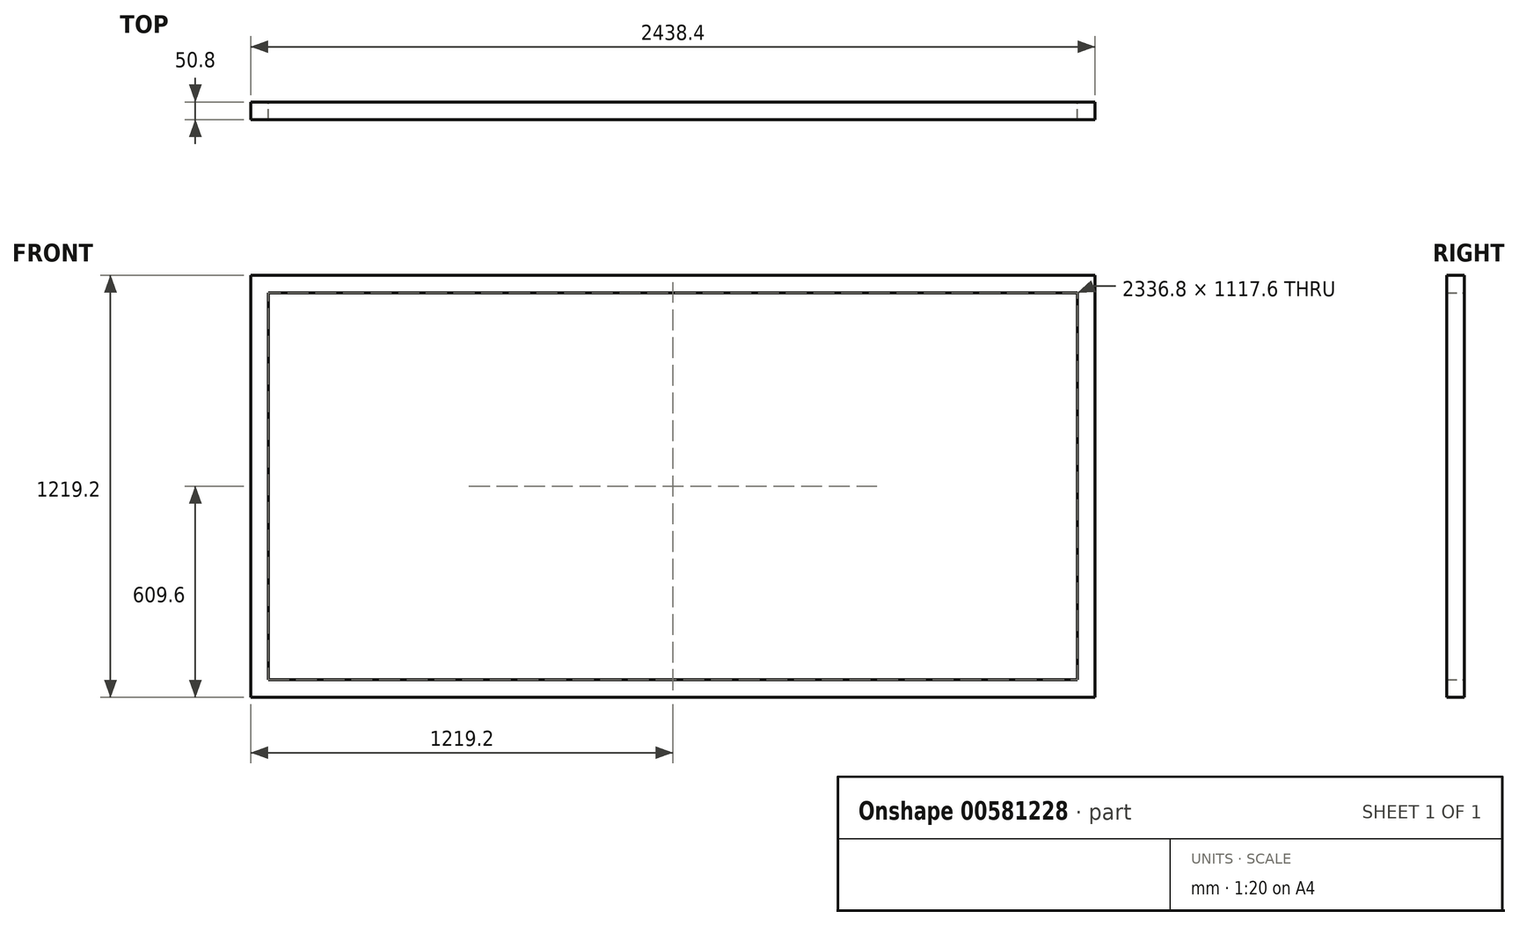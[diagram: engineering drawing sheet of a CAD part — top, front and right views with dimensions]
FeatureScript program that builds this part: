
annotation { "Feature Type Name" : "Feature", "Feature Type Description" : "" }
export const myFeature = defineFeature(function(context is Context, id is Id, definition is map)
    precondition{}
    {
        {
            var Q0;
            Q0=qCreatedBy(makeId("Front.planeOp"),FACE);
            var sketch = newSketch(context, id + "F0", { "sketchPlane" : qUnion([Q0])});
            skLineSegment(sketch, "E0.bottom", {"start": v(1219.2, -609.6) * mm, "end": v(-1219.2, -609.6) * mm});
            skLineSegment(sketch, "E0.top", {"start": v(1219.2, 609.6) * mm, "end": v(-1219.2, 609.6) * mm});
            skLineSegment(sketch, "E0.left", {"start": v(1219.2, -609.6) * mm, "end": v(1219.2, 609.6) * mm});
            skLineSegment(sketch, "E0.right", {"start": v(-1219.2, -609.6) * mm, "end": v(-1219.2, 609.6) * mm});
            skPoint(sketch, "E0.middle", {"position": v(0, 0) * mm});
            skLineSegment(sketch, "E1.bottom", {"start": v(1168.4, 558.8) * mm, "end": v(-1168.4, 558.8) * mm});
            skLineSegment(sketch, "E1.top", {"start": v(1168.4, -558.8) * mm, "end": v(-1168.4, -558.8) * mm});
            skLineSegment(sketch, "E1.left", {"start": v(1168.4, 558.8) * mm, "end": v(1168.4, -558.8) * mm});
            skLineSegment(sketch, "E1.right", {"start": v(-1168.4, 558.8) * mm, "end": v(-1168.4, -558.8) * mm});
            skSolve(sketch);
        }
        {
            var Q0;
            Q0=makeQuery(id+"F0.imprint","IMPRINT",FACE,{"disambiguationData":[TD([[makeQuery(id+"F0.imprint","IMPRINT",EDGE,{"derivedFrom":sQuery(id+"F0.wireOp",EDGE,"E0.bottom")}),-1.0]])]});
            extrude(context, id + "F1", {"entities" : qUnion([Q0]), "depth" : 50.8 * mm, "offsetDistance" : 25.4 * mm});
        }
    });
